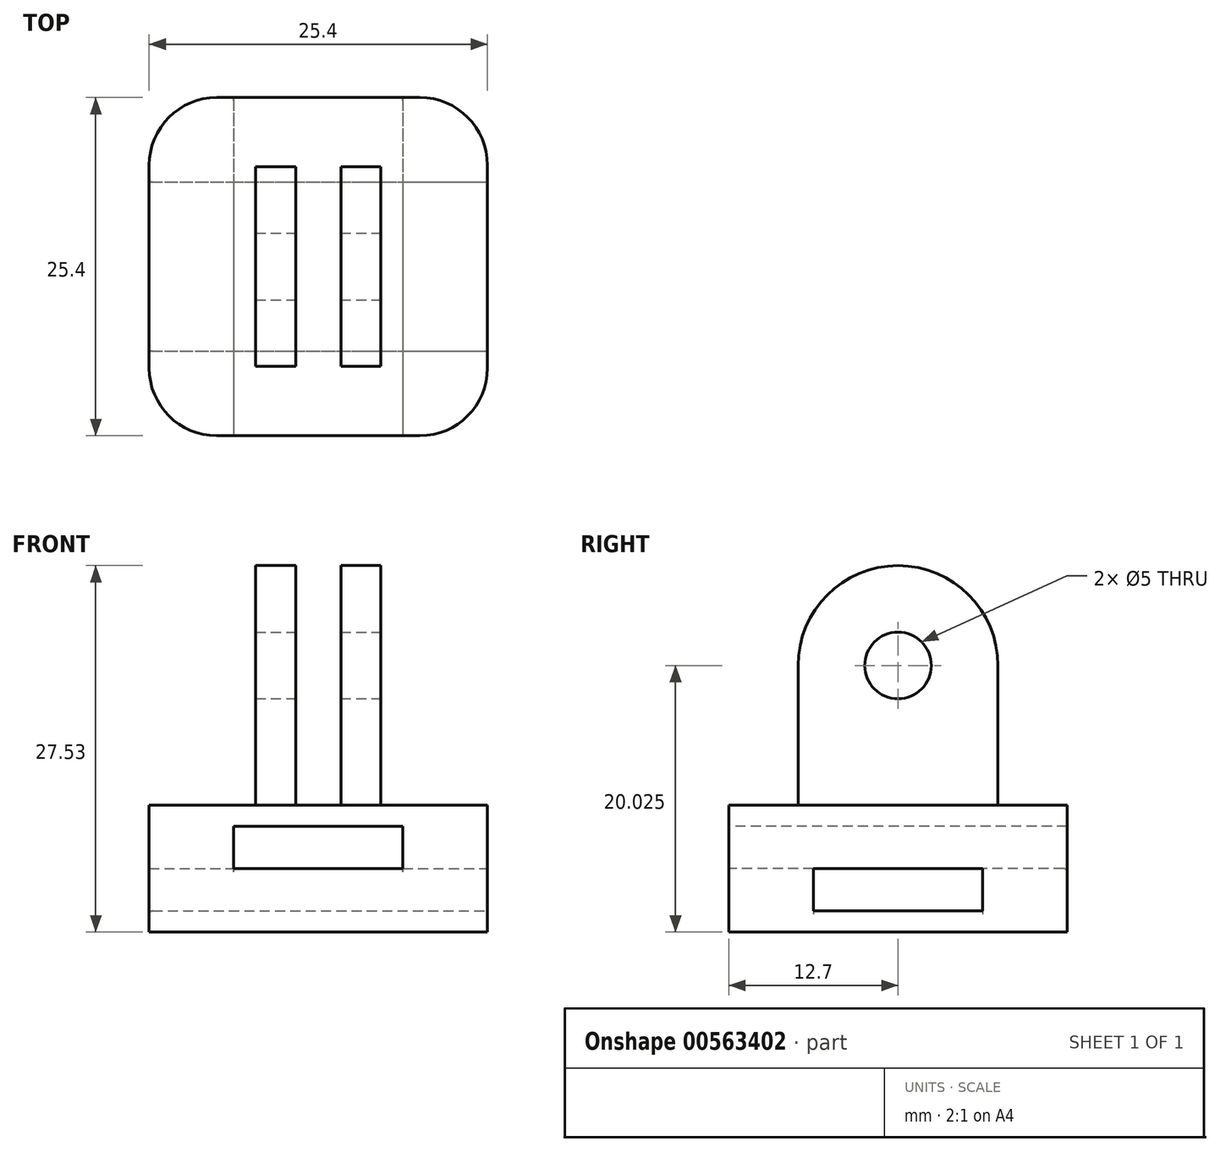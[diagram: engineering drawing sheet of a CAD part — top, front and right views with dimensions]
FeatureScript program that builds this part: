
annotation { "Feature Type Name" : "Feature", "Feature Type Description" : "" }
export const myFeature = defineFeature(function(context is Context, id is Id, definition is map)
    precondition{}
    {
        {
            var Q0;
            Q0=qCreatedBy(makeId("Top.planeOp"),FACE);
            var sketch = newSketch(context, id + "F0", { "sketchPlane" : qUnion([Q0])});
            skLineSegment(sketch, "E0.bottom", {"start": v(-12.7, 12.7) * mm, "end": v(12.7, 12.7) * mm});
            skLineSegment(sketch, "E0.top", {"start": v(-12.7, -12.7) * mm, "end": v(12.7, -12.7) * mm});
            skLineSegment(sketch, "E0.left", {"start": v(-12.7, 12.7) * mm, "end": v(-12.7, -12.7) * mm});
            skLineSegment(sketch, "E0.right", {"start": v(12.7, 12.7) * mm, "end": v(12.7, -12.7) * mm});
            skPoint(sketch, "E0.middle", {"position": v(0, 0) * mm});
            skSolve(sketch);
        }
        {
            var Q0;
            Q0=makeQuery(id+"F0.imprint","IMPRINT",FACE,{"disambiguationData":[TD([[makeQuery(id+"F0.imprint","IMPRINT",EDGE,{"derivedFrom":sQuery(id+"F0.wireOp",EDGE,"E0.bottom")}),-1.0]])]});
            extrude(context, id + "F1", {"entities" : qUnion([Q0]), "depth" : 9.52 * mm, "offsetDistance" : 25.4 * mm});
        }
        {
            var Q0;
            Q0=makeQuery(id+"F1.opExtrude","CAP_FACE",FACE,{"disambiguationData":[OSD([sQuery(id+"F0.wireOp",EDGE,"E0.bottom"),sQuery(id+"F0.wireOp",EDGE,"E0.top"),sQuery(id+"F0.wireOp",EDGE,"E0.left"),sQuery(id+"F0.wireOp",EDGE,"E0.right")])],"isStart":false});
            var sketch = newSketch(context, id + "F2", { "sketchPlane" : qUnion([Q0])});
            skLineSegment(sketch, "E1.bottom", {"start": v(-4.7, 7.5) * mm, "end": v(-1.7, 7.5) * mm});
            skLineSegment(sketch, "E1.top", {"start": v(-4.7, -7.5) * mm, "end": v(-1.7, -7.5) * mm});
            skLineSegment(sketch, "E1.left", {"start": v(-4.7, 7.5) * mm, "end": v(-4.7, -7.5) * mm});
            skLineSegment(sketch, "E1.right", {"start": v(-1.7, 7.5) * mm, "end": v(-1.7, -7.5) * mm});
            skPoint(sketch, "E1.middle", {"position": v(-3.2, 0) * mm});
            skLineSegment(sketch, "E2.MirrorCS", {"start": v(4.7, 7.5) * mm, "end": v(1.7, 7.5) * mm});
            skLineSegment(sketch, "E3.MirrorCS", {"start": v(4.7, 7.5) * mm, "end": v(4.7, -7.5) * mm});
            skLineSegment(sketch, "E4.MirrorCS", {"start": v(1.7, 7.5) * mm, "end": v(1.7, -7.5) * mm});
            skLineSegment(sketch, "E5.MirrorCS", {"start": v(4.7, -7.5) * mm, "end": v(1.7, -7.5) * mm});
            skSolve(sketch);
        }
        {
            var Q0;
            Q0=makeQuery(id+"F2.imprint","IMPRINT",FACE,{"disambiguationData":[TD([[makeQuery(id+"F2.imprint","IMPRINT",EDGE,{"derivedFrom":sQuery(id+"F2.wireOp",EDGE,"E1.bottom")}),-1.0]])]});
            var Q1;
            Q1=makeQuery(id+"F2.imprint","IMPRINT",FACE,{"disambiguationData":[TD([[makeQuery(id+"F2.imprint","IMPRINT",EDGE,{"derivedFrom":sQuery(id+"F2.wireOp",EDGE,"E2.MirrorCS")}),1.0]])]});
            extrude(context, id + "F3", {"entities" : qUnion([Q0, Q1]), "operationType" : NewBodyOperationType.ADD, "depth" : 18 * mm, "offsetDistance" : 25.4 * mm});
        }
        {
            var Q0;
            Q0=makeQuery(id+"F3.opExtrude","CAP_EDGE",EDGE,{"disambiguationData":[OSD([sQuery(id+"F2.wireOp",EDGE,"E2.MirrorCS")])],"isStart":false});
            var Q1;
            Q1=makeQuery(id+"F3.opExtrude","CAP_EDGE",EDGE,{"disambiguationData":[OSD([sQuery(id+"F2.wireOp",EDGE,"E5.MirrorCS")])],"isStart":false});
            var Q2;
            Q2=makeQuery(id+"F3.opExtrude","CAP_EDGE",EDGE,{"disambiguationData":[OSD([sQuery(id+"F2.wireOp",EDGE,"E1.bottom")])],"isStart":false});
            var Q3;
            Q3=makeQuery(id+"F3.opExtrude","CAP_EDGE",EDGE,{"disambiguationData":[OSD([sQuery(id+"F2.wireOp",EDGE,"E1.top")])],"isStart":false});
            fillet(context, id + "F4", {"entities" : qUnion([Q0, Q1, Q2, Q3]), "radius" : 7.5 * mm, "tangentPropagation" : true, "allowEdgeOverflow" : false});
        }
        {
            var Q0;
            Q0=makeQuery(id+"F1.opExtrude","SWEPT_FACE",FACE,{"disambiguationData":[OSD([sQuery(id+"F0.wireOp",EDGE,"E0.right")])]});
            var sketch = newSketch(context, id + "F5", { "sketchPlane" : qUnion([Q0])});
            skLineSegment(sketch, "E6.bottom", {"start": v(-6.35, 4.76) * mm, "end": v(6.35, 4.76) * mm});
            skLineSegment(sketch, "E6.top", {"start": v(-6.35, 1.59) * mm, "end": v(6.35, 1.59) * mm});
            skLineSegment(sketch, "E6.left", {"start": v(-6.35, 4.76) * mm, "end": v(-6.35, 1.59) * mm});
            skLineSegment(sketch, "E6.right", {"start": v(6.35, 4.76) * mm, "end": v(6.35, 1.59) * mm});
            skPoint(sketch, "E6.middle", {"position": v(0, 3.18) * mm});
            skSolve(sketch);
        }
        {
            var Q0;
            Q0=makeQuery(id+"F5.imprint","IMPRINT",FACE,{"disambiguationData":[TD([[makeQuery(id+"F5.imprint","IMPRINT",EDGE,{"derivedFrom":sQuery(id+"F5.wireOp",EDGE,"E6.bottom")}),-1.0]])]});
            extrude(context, id + "F6", {"entities" : qUnion([Q0]), "operationType" : NewBodyOperationType.REMOVE, "endBound" : BoundingType.THROUGH_ALL, "oppositeDirection" : true, "depth" : 25.4 * mm, "offsetDistance" : 25.4 * mm});
        }
        {
            var Q0;
            Q0=makeQuery(id+"F1.opExtrude","SWEPT_FACE",FACE,{"disambiguationData":[OSD([sQuery(id+"F0.wireOp",EDGE,"E0.top")])]});
            var sketch = newSketch(context, id + "F7", { "sketchPlane" : qUnion([Q0])});
            skLineSegment(sketch, "E7.bottom", {"start": v(-6.35, 7.94) * mm, "end": v(6.35, 7.94) * mm});
            skLineSegment(sketch, "E7.top", {"start": v(-6.35, 4.76) * mm, "end": v(6.35, 4.76) * mm});
            skLineSegment(sketch, "E7.left", {"start": v(-6.35, 7.94) * mm, "end": v(-6.35, 4.76) * mm});
            skLineSegment(sketch, "E7.right", {"start": v(6.35, 7.94) * mm, "end": v(6.35, 4.76) * mm});
            skPoint(sketch, "E7.middle", {"position": v(0, 6.35) * mm});
            skSolve(sketch);
        }
        {
            var Q0;
            Q0=makeQuery(id+"F7.imprint","IMPRINT",FACE,{"disambiguationData":[TD([[makeQuery(id+"F7.imprint","IMPRINT",EDGE,{"derivedFrom":sQuery(id+"F7.wireOp",EDGE,"E7.bottom")}),-1.0]])]});
            extrude(context, id + "F8", {"entities" : qUnion([Q0]), "operationType" : NewBodyOperationType.REMOVE, "endBound" : BoundingType.THROUGH_ALL, "oppositeDirection" : true, "depth" : 25.4 * mm, "offsetDistance" : 25.4 * mm});
        }
        {
            var Q0;
            Q0=makeQuery(id+"F3.opExtrude","SWEPT_FACE",FACE,{"disambiguationData":[OSD([sQuery(id+"F2.wireOp",EDGE,"E3.MirrorCS")])]});
            var sketch = newSketch(context, id + "F9", { "sketchPlane" : qUnion([Q0])});
            skPoint(sketch, "E8", {"position": v(0, 20.03) * mm});
            skSolve(sketch);
        }
        {
            var Q0;
            Q0=sQuery(id+"F9.wireOp",VERTEX,"E8");
            var Q1;
            Q1=makeQuery(id+"F1.opExtrude","SWEPT_BODY",BODY,{"disambiguationData":[OSD([sQuery(id+"F0.wireOp",EDGE,"E0.bottom"),sQuery(id+"F0.wireOp",EDGE,"E0.top"),sQuery(id+"F0.wireOp",EDGE,"E0.left"),sQuery(id+"F0.wireOp",EDGE,"E0.right")])]});
            hole(context, id + "F10", {"style" : HoleStyle.SIMPLE, "endStyle" : HoleEndStyle.THROUGH, "holeDiameter" : 5 * mm, "majorDiameter" : 6.35 * mm, "isTappedThrough" : true, "tappedDepth" : 12.7 * mm, "tapClearance" : 3, "locations" : qUnion([Q0]), "scope" : qUnion([Q1])});
        }
        {
            var Q0;
            Q0=makeQuery(id+"F1.opExtrude","SWEPT_EDGE",EDGE,{"disambiguationData":[OSD([sQuery(id+"F0.wireOp",EDGE,"E0.top"),sQuery(id+"F0.wireOp",EDGE,"E0.right")])]});
            var Q1;
            Q1=makeQuery(id+"F1.opExtrude","SWEPT_EDGE",EDGE,{"disambiguationData":[OSD([sQuery(id+"F0.wireOp",EDGE,"E0.top"),sQuery(id+"F0.wireOp",EDGE,"E0.left")])]});
            var Q2;
            Q2=makeQuery(id+"F1.opExtrude","SWEPT_EDGE",EDGE,{"disambiguationData":[OSD([sQuery(id+"F0.wireOp",EDGE,"E0.bottom"),sQuery(id+"F0.wireOp",EDGE,"E0.right")])]});
            var Q3;
            Q3=makeQuery(id+"F1.opExtrude","SWEPT_EDGE",EDGE,{"disambiguationData":[OSD([sQuery(id+"F0.wireOp",EDGE,"E0.bottom"),sQuery(id+"F0.wireOp",EDGE,"E0.left")])]});
            fillet(context, id + "F11", {"entities" : qUnion([Q0, Q1, Q2, Q3]), "radius" : 5.08 * mm, "tangentPropagation" : true, "allowEdgeOverflow" : false});
        }
        {
            var Q0;
            Q0=makeQuery(id+"F8.boolean.opBoolean","COPY",EDGE,{"derivedFrom":makeQuery(id+"F8.opExtrude","CAP_EDGE",EDGE,{"disambiguationData":[OSD([sQuery(id+"F7.wireOp",EDGE,"E7.top")])],"isStart":true})});
            var Q1;
            Q1=makeQuery(id+"F6.boolean.opBoolean","COPY",EDGE,{"derivedFrom":makeQuery(id+"F6.opExtrude","CAP_EDGE",EDGE,{"disambiguationData":[OSD([sQuery(id+"F5.wireOp",EDGE,"E6.top")])],"isStart":true})});
            var Q2;
            Q2=makeQuery(id+"F8.boolean.opBoolean","INTERSECT",EDGE,{"derivedFrom":[makeQuery(id+"F1.opExtrude","SWEPT_FACE",FACE,{"disambiguationData":[OSD([sQuery(id+"F0.wireOp",EDGE,"E0.bottom")])]}),makeQuery(id+"F8.opExtrude","SWEPT_FACE",FACE,{"disambiguationData":[OSD([sQuery(id+"F7.wireOp",EDGE,"E7.top")])]})]});
            var Q3;
            Q3=makeQuery(id+"F6.boolean.opBoolean","INTERSECT",EDGE,{"derivedFrom":[makeQuery(id+"F1.opExtrude","SWEPT_FACE",FACE,{"disambiguationData":[OSD([sQuery(id+"F0.wireOp",EDGE,"E0.left")])]}),makeQuery(id+"F6.opExtrude","SWEPT_FACE",FACE,{"disambiguationData":[OSD([sQuery(id+"F5.wireOp",EDGE,"E6.top")])]})]});
            fillet(context, id + "F12", {"entities" : qUnion([Q0, Q1, Q2, Q3]), "radius" : 0.25 * mm, "tangentPropagation" : true, "allowEdgeOverflow" : false});
        }
    });
